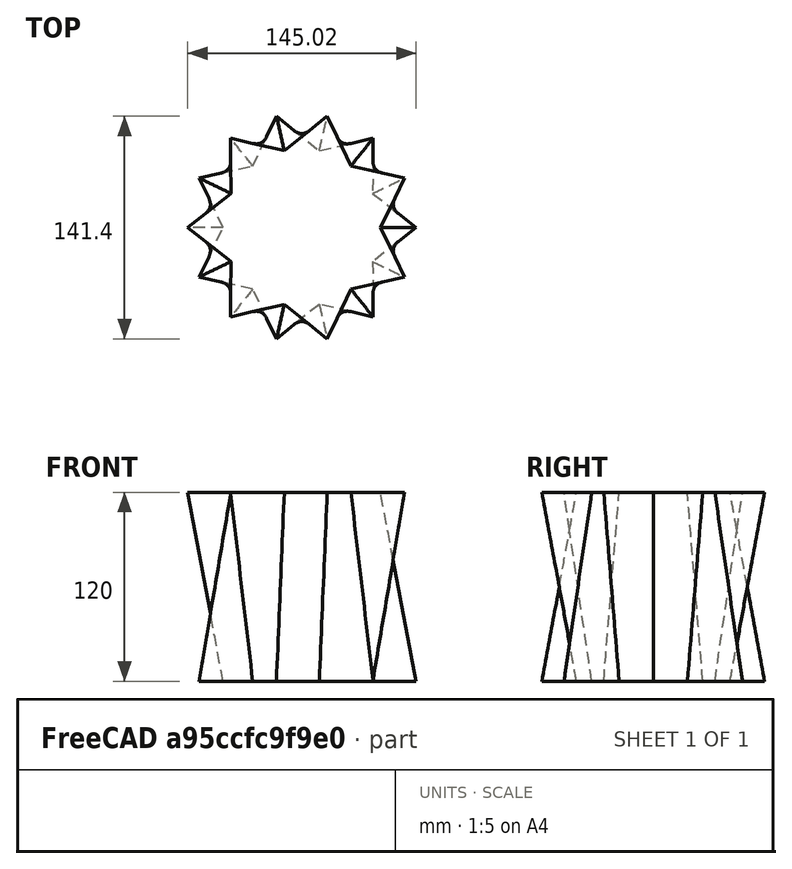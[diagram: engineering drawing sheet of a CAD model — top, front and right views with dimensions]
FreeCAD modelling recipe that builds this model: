
FCSTD DOCUMENT  (FreeCAD 0.19R22846 (Git))
Label: laterne_max
License: All rights reserved
LicenseURL: http://en.wikipedia.org/wiki/All_rights_reserved
objects: Sketcher::SketchObject×2, PartDesign::AdditiveLoft×1, PartDesign::Body×1
note: 5 computed .brp shape members not serialized (recipe doc carries the construction recipe); baked Part::Feature solids carry a one-line shape summary decoded from their .brp

FEATURE [Sketcher::SketchObject] Sketch  label="sk_boden"
  MapMode = 5
  Support = -> [XY_Plane]
  sketch-geometry (22):
    g0: LineSegment StartX=-50 StartY=-1.137e-13 StartZ=0 EndX=-65.3329 EndY=31.4627 EndZ=0
    g1: LineSegment StartX=-65.3329 StartY=31.4627 StartZ=0 EndX=-31.1745 EndY=39.0916 EndZ=0
    g2: LineSegment StartX=-31.1745 StartY=39.0916 StartZ=0 EndX=-16.1359 EndY=70.696 EndZ=0
    g3: LineSegment StartX=-16.1359 StartY=70.696 StartZ=0 EndX=11.126 EndY=48.7464 EndZ=0
    g4: LineSegment StartX=11.126 StartY=48.7464 StartZ=0 EndX=45.2118 EndY=56.6938 EndZ=0
    g5: LineSegment StartX=45.2118 StartY=56.6938 StartZ=0 EndX=45.0484 EndY=21.6942 EndZ=0
    g6: LineSegment StartX=45.0484 StartY=21.6942 StartZ=0 EndX=72.5141 EndY=0 EndZ=0
    g7: LineSegment StartX=72.5141 StartY=0 StartZ=0 EndX=45.0484 EndY=-21.6942 EndZ=0
    g8: LineSegment StartX=45.0484 StartY=-21.6942 StartZ=0 EndX=45.2118 EndY=-56.6938 EndZ=0
    g9: LineSegment StartX=45.2118 StartY=-56.6938 StartZ=0 EndX=11.126 EndY=-48.7464 EndZ=0
    g10: LineSegment StartX=11.126 StartY=-48.7464 StartZ=0 EndX=-16.1359 EndY=-70.696 EndZ=0
    g11: LineSegment StartX=-16.1359 StartY=-70.696 StartZ=0 EndX=-31.1745 EndY=-39.0916 EndZ=0
    g12: LineSegment StartX=-31.1745 StartY=-39.0916 StartZ=0 EndX=-65.3329 EndY=-31.4627 EndZ=0
    g13: LineSegment StartX=-65.3329 StartY=-31.4627 StartZ=0 EndX=-50 EndY=-1.172e-13 EndZ=0
    g14: Circle [constr] CenterX=0 CenterY=0 CenterZ=0 NormalX=0 NormalY=0 NormalZ=1 AngleXU=0 Radius=50
    g15: LineSegment [constr] StartX=-50 StartY=-1.137e-13 StartZ=0 EndX=-31.1745 EndY=-39.0916 EndZ=0
    g16: LineSegment [constr] StartX=-31.1745 StartY=-39.0916 StartZ=0 EndX=11.126 EndY=-48.7464 EndZ=0
    g17: LineSegment [constr] StartX=11.126 StartY=-48.7464 StartZ=0 EndX=45.0484 EndY=-21.6942 EndZ=0
    g18: LineSegment [constr] StartX=45.0484 StartY=-21.6942 StartZ=0 EndX=45.0484 EndY=21.6942 EndZ=0
    g19: LineSegment [constr] StartX=45.0484 StartY=21.6942 StartZ=0 EndX=11.126 EndY=48.7464 EndZ=0
    g20: LineSegment [constr] StartX=11.126 StartY=48.7464 StartZ=0 EndX=-31.1745 EndY=39.0916 EndZ=0
    g21: LineSegment [constr] StartX=-31.1745 StartY=39.0916 StartZ=0 EndX=-50 EndY=-1.137e-13 EndZ=0
  constraints (58):
    c: Coincident(g0,g1)
    c: Coincident(g1,g2)
    c: Coincident(g2,g3)
    c: Coincident(g3,g4)
    c: Coincident(g4,g5)
    c: Coincident(g5,g6)
    c: Coincident(g6,g7)
    c: Coincident(g7,g8)
    c: Coincident(g8,g9)
    c: Coincident(g9,g10)
    c: Coincident(g10,g11)
    c: Coincident(g11,g12)
    c: Coincident(g12,g13)
    c: Coincident(g13,g0)
    c: Equal(g13,g0)
    c: Equal(g0,g1)
    c: Equal(g1,g2)
    c: Equal(g2,g3)
    c: Equal(g3,g4)
    c: Equal(g4,g5)
    c: Equal(g5,g6)
    c: Equal(g6,g7)
    c: Equal(g7,g8)
    c: Equal(g8,g9)
    c: Equal(g9,g10)
    c: Equal(g10,g11)
    c: Equal(g11,g12)
    c: Coincident(g14,g-1)
    c: PointOnObject(g5,g14)
    c: PointOnObject(g7,g14)
    c: PointOnObject(g9,g14)
    c: PointOnObject(g11,g14)
    c: PointOnObject(g0,g14)
    c: PointOnObject(g1,g14)
    c: PointOnObject(g3,g14)
    c: Coincident(g0,g15)
    c: Coincident(g15,g11)
    c: Coincident(g15,g16)
    c: Coincident(g16,g9)
    c: Coincident(g16,g17)
    c: Coincident(g17,g7)
    c: Coincident(g17,g18)
    c: Coincident(g18,g5)
    c: Coincident(g18,g19)
    c: Coincident(g19,g3)
    c: Coincident(g19,g20)
    c: Coincident(g20,g1)
    c: Coincident(g20,g21)
    c: Coincident(g21,g15)
    c: Equal(g21,g15)
    c: Equal(g15,g16)
    c: Equal(g16,g17)
    c: Equal(g17,g18)
    c: Equal(g18,g19)
    c: Equal(g19,g20)
    c: Radius(g14) = 50
    c: Distance(g13) = 35
    c: PointOnObject(g6,g-1)
FEATURE [Sketcher::SketchObject] Sketch001  label="sk_top"
  AttachmentOffset = pos=(0,0,120) rot=(0,0,1;0rad)
  MapMode = 5
  Placement = pos=(0,0,120) rot=(0,0,1;0rad)
  Support = -> [XY_Plane]
  sketch-geometry (22):
    g0: LineSegment StartX=-45.0484 StartY=21.6942 StartZ=0 EndX=-45.2118 EndY=56.6938 EndZ=0
    g1: LineSegment StartX=-45.2118 StartY=56.6938 StartZ=0 EndX=-11.126 EndY=48.7464 EndZ=0
    g2: LineSegment StartX=-11.126 StartY=48.7464 StartZ=0 EndX=16.1359 EndY=70.696 EndZ=0
    g3: LineSegment StartX=16.1359 StartY=70.696 StartZ=0 EndX=31.1745 EndY=39.0916 EndZ=0
    g4: LineSegment StartX=31.1745 StartY=39.0916 StartZ=0 EndX=65.3329 EndY=31.4627 EndZ=0
    g5: LineSegment StartX=65.3329 StartY=31.4627 StartZ=0 EndX=50 EndY=-7.1e-15 EndZ=0
    g6: LineSegment StartX=50 StartY=-7.1e-15 StartZ=0 EndX=65.3329 EndY=-31.4627 EndZ=0
    g7: LineSegment StartX=65.3329 StartY=-31.4627 StartZ=0 EndX=31.1745 EndY=-39.0916 EndZ=0
    g8: LineSegment StartX=31.1745 StartY=-39.0916 StartZ=0 EndX=16.1359 EndY=-70.696 EndZ=0
    g9: LineSegment StartX=16.1359 StartY=-70.696 StartZ=0 EndX=-11.126 EndY=-48.7464 EndZ=0
    g10: LineSegment StartX=-11.126 StartY=-48.7464 StartZ=0 EndX=-45.2118 EndY=-56.6938 EndZ=0
    g11: LineSegment StartX=-45.2118 StartY=-56.6938 StartZ=0 EndX=-45.0484 EndY=-21.6942 EndZ=0
    g12: LineSegment StartX=-45.0484 StartY=-21.6942 StartZ=0 EndX=-72.5141 EndY=0 EndZ=0
    g13: LineSegment StartX=-72.5141 StartY=0 StartZ=0 EndX=-45.0484 EndY=21.6942 EndZ=0
    g14: Circle [constr] CenterX=0 CenterY=0 CenterZ=0 NormalX=0 NormalY=0 NormalZ=1 AngleXU=0 Radius=50
    g15: LineSegment [constr] StartX=-45.0484 StartY=21.6942 StartZ=0 EndX=-45.0484 EndY=-21.6942 EndZ=0
    g16: LineSegment [constr] StartX=-45.0484 StartY=-21.6942 StartZ=0 EndX=-11.126 EndY=-48.7464 EndZ=0
    g17: LineSegment [constr] StartX=-11.126 StartY=-48.7464 StartZ=0 EndX=31.1745 EndY=-39.0916 EndZ=0
    g18: LineSegment [constr] StartX=31.1745 StartY=-39.0916 StartZ=0 EndX=50 EndY=-7.1e-15 EndZ=0
    g19: LineSegment [constr] StartX=50 StartY=-7.1e-15 StartZ=0 EndX=31.1745 EndY=39.0916 EndZ=0
    g20: LineSegment [constr] StartX=31.1745 StartY=39.0916 StartZ=0 EndX=-11.126 EndY=48.7464 EndZ=0
    g21: LineSegment [constr] StartX=-11.126 StartY=48.7464 StartZ=0 EndX=-45.0484 EndY=21.6942 EndZ=0
  constraints (58):
    c: Coincident(g0,g1)
    c: Coincident(g1,g2)
    c: Coincident(g2,g3)
    c: Coincident(g3,g4)
    c: Coincident(g4,g5)
    c: Coincident(g5,g6)
    c: Coincident(g6,g7)
    c: Coincident(g7,g8)
    c: Coincident(g8,g9)
    c: Coincident(g9,g10)
    c: Coincident(g10,g11)
    c: Coincident(g11,g12)
    c: Coincident(g12,g13)
    c: Coincident(g13,g0)
    c: Equal(g13,g0)
    c: Equal(g0,g1)
    c: Equal(g1,g2)
    c: Equal(g2,g3)
    c: Equal(g3,g4)
    c: Equal(g4,g5)
    c: Equal(g5,g6)
    c: Equal(g6,g7)
    c: Equal(g7,g8)
    c: Equal(g8,g9)
    c: Equal(g9,g10)
    c: Equal(g10,g11)
    c: Equal(g11,g12)
    c: Coincident(g14,g-1)
    c: PointOnObject(g5,g14)
    c: PointOnObject(g7,g14)
    c: PointOnObject(g9,g14)
    c: PointOnObject(g11,g14)
    c: PointOnObject(g0,g14)
    c: PointOnObject(g1,g14)
    c: PointOnObject(g3,g14)
    c: Coincident(g0,g15)
    c: Coincident(g15,g11)
    c: Coincident(g15,g16)
    c: Coincident(g16,g9)
    c: Coincident(g16,g17)
    c: Coincident(g17,g7)
    c: Coincident(g17,g18)
    c: Coincident(g18,g5)
    c: Coincident(g18,g19)
    c: Coincident(g19,g3)
    c: Coincident(g19,g20)
    c: Coincident(g20,g1)
    c: Coincident(g20,g21)
    c: Coincident(g21,g15)
    c: Equal(g21,g15)
    c: Equal(g15,g16)
    c: Equal(g16,g17)
    c: Equal(g17,g18)
    c: Equal(g18,g19)
    c: Equal(g19,g20)
    c: Radius(g14) = 50
    c: Distance(g13) = 35
    c: PointOnObject(g12,g-1)
FEATURE [PartDesign::AdditiveLoft] AdditiveLoft
  Closed = false
  Profile = -> Sketch
  Refine = true
  Ruled = false
  Sections = -> [Sketch001]
FEATURE [PartDesign::Body] Body
  Group = -> [Sketch,Sketch001,AdditiveLoft]
  Origin = -> Origin
  Tip = -> AdditiveLoft
